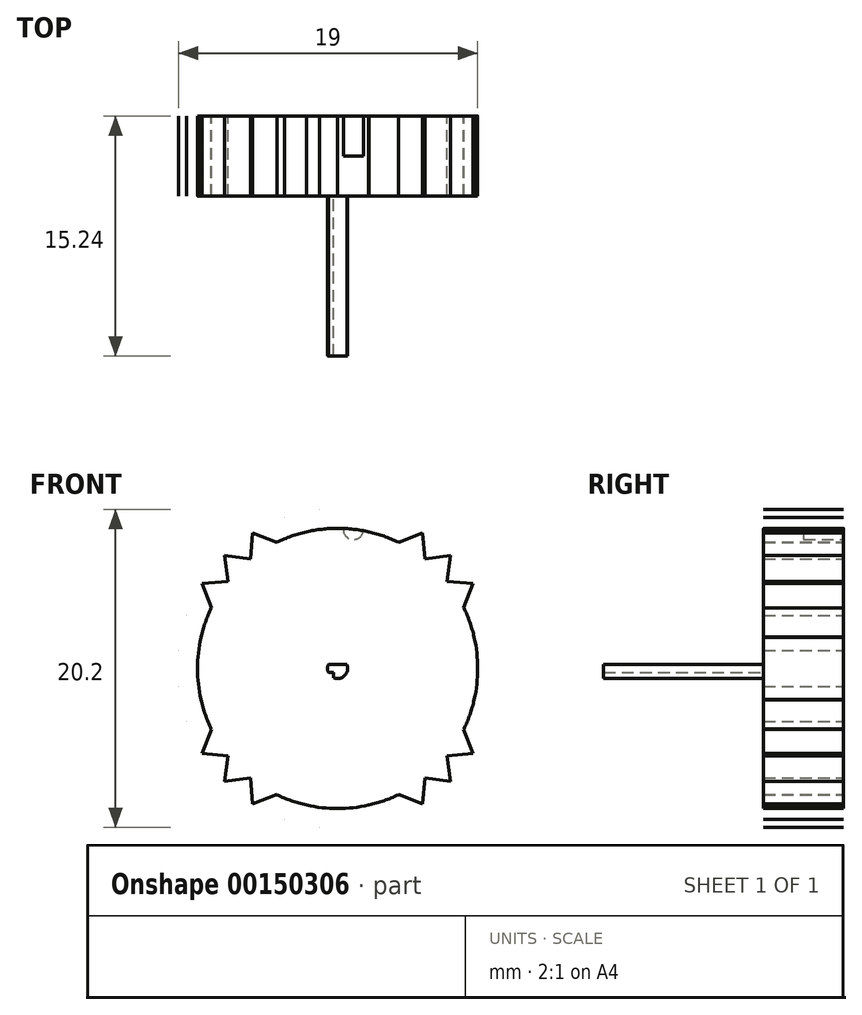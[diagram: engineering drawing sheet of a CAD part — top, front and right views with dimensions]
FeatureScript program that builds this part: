
annotation { "Feature Type Name" : "Feature", "Feature Type Description" : "" }
export const myFeature = defineFeature(function(context is Context, id is Id, definition is map)
    precondition{}
    {
        {
            var Q0;
            Q0=qCreatedBy(makeId("Front.planeOp"),FACE);
            var sketch = newSketch(context, id + "F0", { "sketchPlane" : qUnion([Q0])});
            skCircle(sketch, "E0", {"center": v(0, 0) * mm, "radius": 10.16 * mm});
            skCircle(sketch, "E1", {"center": v(0, 0) * mm, "radius": 8.9 * mm});
            skLineSegment(sketch, "E2", {"start": v(0, 0) * mm, "end": v(0, 8.9) * mm});
            skLineSegment(sketch, "E3", {"start": v(0, 8.9) * mm, "end": v(0, -8.9) * mm});
            skLineSegment(sketch, "E4", {"start": v(0, -8.9) * mm, "end": v(-1.14, -10.1) * mm});
            skLineSegment(sketch, "E5", {"start": v(-1.14, -10.1) * mm, "end": v(-1.98, -8.67) * mm});
            skLineSegment(sketch, "E6", {"start": v(-1.98, -8.67) * mm, "end": v(0, 0) * mm});
            skLineSegment(sketch, "E7", {"start": v(-1.14, -10.1) * mm, "end": v(0, 0) * mm});
            skLineSegment(sketch, "E8", {"start": v(0, 0) * mm, "end": v(-3.36, -9.59) * mm});
            skLineSegment(sketch, "E9", {"start": v(0, 0) * mm, "end": v(-3.86, -8) * mm});
            skLineSegment(sketch, "E10", {"start": v(-3.86, -8) * mm, "end": v(-3.36, -9.59) * mm});
            skLineSegment(sketch, "E11", {"start": v(-1.98, -8.67) * mm, "end": v(-3.36, -9.59) * mm});
            skLineSegment(sketch, "E12.MirrorCS", {"start": v(-3.86, -8) * mm, "end": v(-5.4, -8.6) * mm});
            skLineSegment(sketch, "E13.MirrorCS", {"start": v(0, 0) * mm, "end": v(-5.4, -8.6) * mm});
            skLineSegment(sketch, "E14.MirrorCS", {"start": v(-5.54, -6.95) * mm, "end": v(-5.4, -8.6) * mm});
            skLineSegment(sketch, "E15.MirrorCS", {"start": v(-7.18, -7.18) * mm, "end": v(-5.54, -6.95) * mm});
            skLineSegment(sketch, "E16.MirrorCS", {"start": v(-5.54, -6.95) * mm, "end": v(0, 0) * mm});
            skLineSegment(sketch, "E17.MirrorCS", {"start": v(-7.18, -7.18) * mm, "end": v(0, 0) * mm});
            skLineSegment(sketch, "E18.MirrorCS", {"start": v(-6.95, -5.54) * mm, "end": v(-7.18, -7.18) * mm});
            skLineSegment(sketch, "E19.MirrorCS", {"start": v(6.95, 5.54) * mm, "end": v(-6.95, -5.54) * mm});
            skLineSegment(sketch, "E20.MirrorCS", {"start": v(-6.95, -5.54) * mm, "end": v(-8.6, -5.4) * mm});
            skLineSegment(sketch, "E21.MirrorCS", {"start": v(-8.6, -5.4) * mm, "end": v(0, 0) * mm});
            skLineSegment(sketch, "E22.MirrorCS", {"start": v(-8.6, -5.4) * mm, "end": v(-8, -3.86) * mm});
            skLineSegment(sketch, "E23.MirrorCS", {"start": v(-8, -3.86) * mm, "end": v(0, 0) * mm});
            skLineSegment(sketch, "E24.MirrorCS", {"start": v(-8, -3.86) * mm, "end": v(-9.59, -3.36) * mm});
            skLineSegment(sketch, "E25.MirrorCS", {"start": v(0, 0) * mm, "end": v(-9.59, -3.36) * mm});
            skLineSegment(sketch, "E26.MirrorCS", {"start": v(-8.67, -1.98) * mm, "end": v(-9.59, -3.36) * mm});
            skLineSegment(sketch, "E27.MirrorCS", {"start": v(0, 0) * mm, "end": v(-8.67, -1.98) * mm});
            skLineSegment(sketch, "E28.MirrorCS", {"start": v(-8.67, -1.98) * mm, "end": v(-10.1, -1.14) * mm});
            skLineSegment(sketch, "E29.MirrorCS", {"start": v(0, 0) * mm, "end": v(-10.1, -1.14) * mm});
            skLineSegment(sketch, "E30.MirrorCS", {"start": v(-8.9, 0) * mm, "end": v(-10.1, -1.14) * mm});
            skLineSegment(sketch, "E31.MirrorCS", {"start": v(-8.9, 0) * mm, "end": v(0, 0) * mm});
            skLineSegment(sketch, "E32.MirrorCS", {"start": v(-10.1, 1.14) * mm, "end": v(-8.9, 0) * mm});
            skLineSegment(sketch, "E33.MirrorCS", {"start": v(-10.1, 1.14) * mm, "end": v(0, 0) * mm});
            skLineSegment(sketch, "E34.MirrorCS", {"start": v(-8.67, 1.98) * mm, "end": v(-10.1, 1.14) * mm});
            skLineSegment(sketch, "E35.MirrorCS", {"start": v(8.67, -1.98) * mm, "end": v(-8.67, 1.98) * mm});
            skLineSegment(sketch, "E36.MirrorCS", {"start": v(-8.67, 1.98) * mm, "end": v(-9.59, 3.36) * mm});
            skLineSegment(sketch, "E37.MirrorCS", {"start": v(-9.59, 3.36) * mm, "end": v(0, 0) * mm});
            skLineSegment(sketch, "E38.MirrorCS", {"start": v(-9.59, 3.36) * mm, "end": v(-8, 3.86) * mm});
            skLineSegment(sketch, "E39.MirrorCS", {"start": v(-8, 3.86) * mm, "end": v(0, 0) * mm});
            skLineSegment(sketch, "E40.MirrorCS", {"start": v(-8, 3.86) * mm, "end": v(-8.6, 5.4) * mm});
            skLineSegment(sketch, "E41.MirrorCS", {"start": v(0, 0) * mm, "end": v(-8.6, 5.4) * mm});
            skLineSegment(sketch, "E42.MirrorCS", {"start": v(-6.95, 5.54) * mm, "end": v(-8.6, 5.4) * mm});
            skLineSegment(sketch, "E43.MirrorCS", {"start": v(0, 0) * mm, "end": v(-6.95, 5.54) * mm});
            skLineSegment(sketch, "E44.MirrorCS", {"start": v(-6.95, 5.54) * mm, "end": v(-7.18, 7.18) * mm});
            skLineSegment(sketch, "E45.MirrorCS", {"start": v(0, 0) * mm, "end": v(-7.18, 7.18) * mm});
            skLineSegment(sketch, "E46.MirrorCS", {"start": v(-5.54, 6.95) * mm, "end": v(-7.18, 7.18) * mm});
            skLineSegment(sketch, "E47.MirrorCS", {"start": v(-5.54, 6.95) * mm, "end": v(0, 0) * mm});
            skLineSegment(sketch, "E48.MirrorCS", {"start": v(-5.4, 8.6) * mm, "end": v(-5.54, 6.95) * mm});
            skLineSegment(sketch, "E49.MirrorCS", {"start": v(-5.4, 8.6) * mm, "end": v(0, 0) * mm});
            skLineSegment(sketch, "E50.MirrorCS", {"start": v(-3.86, 8) * mm, "end": v(-5.4, 8.6) * mm});
            skLineSegment(sketch, "E51.MirrorCS", {"start": v(3.86, -8) * mm, "end": v(-3.86, 8) * mm});
            skLineSegment(sketch, "E52.MirrorCS", {"start": v(-3.86, 8) * mm, "end": v(-3.36, 9.59) * mm});
            skLineSegment(sketch, "E53.MirrorCS", {"start": v(-3.36, 9.59) * mm, "end": v(0, 0) * mm});
            skLineSegment(sketch, "E54.MirrorCS", {"start": v(-3.36, 9.59) * mm, "end": v(-1.98, 8.67) * mm});
            skLineSegment(sketch, "E55.MirrorCS", {"start": v(-1.98, 8.67) * mm, "end": v(0, 0) * mm});
            skLineSegment(sketch, "E56.MirrorCS", {"start": v(-1.98, 8.67) * mm, "end": v(-1.14, 10.1) * mm});
            skLineSegment(sketch, "E57.MirrorCS", {"start": v(0, 0) * mm, "end": v(-1.14, 10.1) * mm});
            skLineSegment(sketch, "E58.MirrorCS", {"start": v(0, 8.89) * mm, "end": v(-1.14, 10.1) * mm});
            skLineSegment(sketch, "E59.MirrorCS", {"start": v(0, 0) * mm, "end": v(0, 8.89) * mm});
            skLineSegment(sketch, "E60.MirrorCS", {"start": v(0, 8.89) * mm, "end": v(1.14, 10.1) * mm});
            skLineSegment(sketch, "E61.MirrorCS", {"start": v(0, 0) * mm, "end": v(1.14, 10.1) * mm});
            skLineSegment(sketch, "E62.MirrorCS", {"start": v(1.98, 8.67) * mm, "end": v(1.14, 10.1) * mm});
            skLineSegment(sketch, "E63.MirrorCS", {"start": v(1.98, 8.67) * mm, "end": v(0, 0) * mm});
            skLineSegment(sketch, "E64.MirrorCS", {"start": v(3.36, 9.59) * mm, "end": v(1.98, 8.67) * mm});
            skLineSegment(sketch, "E65.MirrorCS", {"start": v(3.36, 9.59) * mm, "end": v(0, 0) * mm});
            skLineSegment(sketch, "E66.MirrorCS", {"start": v(3.86, 8) * mm, "end": v(3.36, 9.59) * mm});
            skLineSegment(sketch, "E67.MirrorCS", {"start": v(-3.86, -8) * mm, "end": v(3.86, 8) * mm});
            skLineSegment(sketch, "E68.MirrorCS", {"start": v(3.86, 8) * mm, "end": v(5.4, 8.6) * mm});
            skLineSegment(sketch, "E69.MirrorCS", {"start": v(5.4, 8.6) * mm, "end": v(0, 0) * mm});
            skLineSegment(sketch, "E70.MirrorCS", {"start": v(5.4, 8.6) * mm, "end": v(5.54, 6.95) * mm});
            skLineSegment(sketch, "E71.MirrorCS", {"start": v(5.54, 6.95) * mm, "end": v(0, 0) * mm});
            skLineSegment(sketch, "E72.MirrorCS", {"start": v(5.54, 6.95) * mm, "end": v(7.18, 7.18) * mm});
            skLineSegment(sketch, "E73.MirrorCS", {"start": v(0, 0) * mm, "end": v(7.18, 7.18) * mm});
            skLineSegment(sketch, "E74.MirrorCS", {"start": v(6.95, 5.54) * mm, "end": v(7.18, 7.18) * mm});
            skLineSegment(sketch, "E75.MirrorCS", {"start": v(6.95, 5.54) * mm, "end": v(8.6, 5.4) * mm});
            skLineSegment(sketch, "E76.MirrorCS", {"start": v(0, 0) * mm, "end": v(8.6, 5.4) * mm});
            skLineSegment(sketch, "E77.MirrorCS", {"start": v(8, 3.86) * mm, "end": v(8.6, 5.4) * mm});
            skLineSegment(sketch, "E78.MirrorCS", {"start": v(8, 3.86) * mm, "end": v(0, 0) * mm});
            skLineSegment(sketch, "E79.MirrorCS", {"start": v(9.59, 3.36) * mm, "end": v(8, 3.86) * mm});
            skLineSegment(sketch, "E80.MirrorCS", {"start": v(9.59, 3.36) * mm, "end": v(0, 0) * mm});
            skLineSegment(sketch, "E81.MirrorCS", {"start": v(8.67, 1.98) * mm, "end": v(9.59, 3.36) * mm});
            skLineSegment(sketch, "E82.MirrorCS", {"start": v(-8.67, -1.98) * mm, "end": v(8.67, 1.98) * mm});
            skLineSegment(sketch, "E83.MirrorCS", {"start": v(8.67, 1.98) * mm, "end": v(10.1, 1.14) * mm});
            skLineSegment(sketch, "E84.MirrorCS", {"start": v(10.1, 1.14) * mm, "end": v(8.9, 0) * mm});
            skLineSegment(sketch, "E85.MirrorCS", {"start": v(10.1, 1.14) * mm, "end": v(0, 0) * mm});
            skLineSegment(sketch, "E86.MirrorCS", {"start": v(8.9, 0) * mm, "end": v(0, 0) * mm});
            skLineSegment(sketch, "E87.MirrorCS", {"start": v(8.9, 0) * mm, "end": v(10.1, -1.14) * mm});
            skLineSegment(sketch, "E88.MirrorCS", {"start": v(0, 0) * mm, "end": v(10.1, -1.14) * mm});
            skLineSegment(sketch, "E89.MirrorCS", {"start": v(8.67, -1.98) * mm, "end": v(10.1, -1.14) * mm});
            skLineSegment(sketch, "E90.MirrorCS", {"start": v(0, 0) * mm, "end": v(8.67, -1.98) * mm});
            skLineSegment(sketch, "E91.MirrorCS", {"start": v(8.67, -1.98) * mm, "end": v(9.59, -3.36) * mm});
            skLineSegment(sketch, "E92.MirrorCS", {"start": v(0, 0) * mm, "end": v(9.59, -3.36) * mm});
            skLineSegment(sketch, "E93.MirrorCS", {"start": v(8, -3.86) * mm, "end": v(9.59, -3.36) * mm});
            skLineSegment(sketch, "E94.MirrorCS", {"start": v(8, -3.86) * mm, "end": v(0, 0) * mm});
            skLineSegment(sketch, "E95.MirrorCS", {"start": v(8.6, -5.4) * mm, "end": v(8, -3.86) * mm});
            skLineSegment(sketch, "E96.MirrorCS", {"start": v(8.6, -5.4) * mm, "end": v(0, 0) * mm});
            skLineSegment(sketch, "E97.MirrorCS", {"start": v(6.95, -5.54) * mm, "end": v(8.6, -5.4) * mm});
            skLineSegment(sketch, "E98.MirrorCS", {"start": v(-6.95, 5.54) * mm, "end": v(6.95, -5.54) * mm});
            skLineSegment(sketch, "E99.MirrorCS", {"start": v(6.95, -5.54) * mm, "end": v(7.18, -7.18) * mm});
            skLineSegment(sketch, "E100.MirrorCS", {"start": v(7.18, -7.18) * mm, "end": v(0, 0) * mm});
            skLineSegment(sketch, "E101.MirrorCS", {"start": v(7.18, -7.18) * mm, "end": v(5.54, -6.95) * mm});
            skLineSegment(sketch, "E102.MirrorCS", {"start": v(5.54, -6.95) * mm, "end": v(0, 0) * mm});
            skLineSegment(sketch, "E103.MirrorCS", {"start": v(5.54, -6.95) * mm, "end": v(5.4, -8.6) * mm});
            skLineSegment(sketch, "E104.MirrorCS", {"start": v(0, 0) * mm, "end": v(5.4, -8.6) * mm});
            skLineSegment(sketch, "E105.MirrorCS", {"start": v(3.86, -8) * mm, "end": v(5.4, -8.6) * mm});
            skLineSegment(sketch, "E106.MirrorCS", {"start": v(0, 0) * mm, "end": v(3.86, -8) * mm});
            skLineSegment(sketch, "E107.MirrorCS", {"start": v(3.86, -8) * mm, "end": v(3.36, -9.59) * mm});
            skLineSegment(sketch, "E108.MirrorCS", {"start": v(1.98, -8.67) * mm, "end": v(3.36, -9.59) * mm});
            skLineSegment(sketch, "E109.MirrorCS", {"start": v(0, 0) * mm, "end": v(3.36, -9.59) * mm});
            skLineSegment(sketch, "E110.MirrorCS", {"start": v(1.98, -8.67) * mm, "end": v(0, 0) * mm});
            skLineSegment(sketch, "E111.MirrorCS", {"start": v(1.14, -10.1) * mm, "end": v(1.98, -8.67) * mm});
            skLineSegment(sketch, "E112.MirrorCS", {"start": v(1.14, -10.1) * mm, "end": v(0, 0) * mm});
            skLineSegment(sketch, "E113.MirrorCS", {"start": v(0, -8.9) * mm, "end": v(1.14, -10.1) * mm});
            skSolve(sketch);
        }
        {
            var Q0;
            {var subQ0=sQuery(id+"F0.wireOp",EDGE,"E51.MirrorCS");Q0=makeQuery(id+"F0.imprint","IMPRINT",FACE,{"disambiguationData":[TD([[makeQuery(id+"F0.imprint","IMPRINT",EDGE,{"derivedFrom":subQ0}),1.0]])]});}
            var Q1;
            {var subQ0=sQuery(id+"F0.wireOp",EDGE,"E47.MirrorCS");Q1=makeQuery(id+"F0.imprint","IMPRINT",FACE,{"disambiguationData":[TD([[makeQuery(id+"F0.imprint","IMPRINT",EDGE,{"derivedFrom":subQ0}),1.0]])]});}
            var Q2;
            {var subQ0=sQuery(id+"F0.wireOp",EDGE,"E48.MirrorCS");Q2=makeQuery(id+"F0.imprint","IMPRINT",FACE,{"disambiguationData":[TD([[makeQuery(id+"F0.imprint","IMPRINT",EDGE,{"derivedFrom":subQ0}),1.0]])]});}
            var Q3;
            {var subQ0=sQuery(id+"F0.wireOp",EDGE,"E50.MirrorCS");Q3=makeQuery(id+"F0.imprint","IMPRINT",FACE,{"disambiguationData":[TD([[makeQuery(id+"F0.imprint","IMPRINT",EDGE,{"derivedFrom":subQ0}),1.0]])]});}
            var Q4;
            {var subQ0=sQuery(id+"F0.wireOp",EDGE,"E52.MirrorCS");Q4=makeQuery(id+"F0.imprint","IMPRINT",FACE,{"disambiguationData":[TD([[makeQuery(id+"F0.imprint","IMPRINT",EDGE,{"derivedFrom":subQ0}),-1.0]])]});}
            var Q5;
            {var subQ0=sQuery(id+"F0.wireOp",EDGE,"E54.MirrorCS");Q5=makeQuery(id+"F0.imprint","IMPRINT",FACE,{"disambiguationData":[TD([[makeQuery(id+"F0.imprint","IMPRINT",EDGE,{"derivedFrom":subQ0}),-1.0]])]});}
            var Q6;
            {var subQ0=sQuery(id+"F0.wireOp",EDGE,"E55.MirrorCS");Q6=makeQuery(id+"F0.imprint","IMPRINT",FACE,{"disambiguationData":[TD([[makeQuery(id+"F0.imprint","IMPRINT",EDGE,{"derivedFrom":subQ0}),-1.0]])]});}
            var Q7;
            {var subQ0=sQuery(id+"F0.wireOp",EDGE,"E51.MirrorCS");Q7=makeQuery(id+"F0.imprint","IMPRINT",FACE,{"disambiguationData":[TD([[makeQuery(id+"F0.imprint","IMPRINT",EDGE,{"derivedFrom":subQ0}),-1.0]])]});}
            var Q8;
            {var subQ1=sQuery(id+"F0.wireOp",EDGE,"E1");var subQ3=sQuery(id+"F0.wireOp",EDGE,"E57.MirrorCS");var subQ4=makeQuery(id+"F0.imprint","INTERSECT",VERTEX,{"derivedFrom":[subQ1,subQ3]});Q8=makeQuery(id+"F0.imprint","IMPRINT",FACE,{"disambiguationData":[TD([[makeQuery(id+"F0.imprint","IMPRINT",EDGE,{"disambiguationData":[TD([[subQ4,1.0]])],"derivedFrom":subQ1}),1.0]])]});}
            var Q9;
            {var subQ0=sQuery(id+"F0.wireOp",EDGE,"E58.MirrorCS");Q9=makeQuery(id+"F0.imprint","IMPRINT",FACE,{"disambiguationData":[TD([[makeQuery(id+"F0.imprint","IMPRINT",EDGE,{"derivedFrom":subQ0}),1.0]])]});}
            var Q10;
            {var subQ0=sQuery(id+"F0.wireOp",EDGE,"E56.MirrorCS");Q10=makeQuery(id+"F0.imprint","IMPRINT",FACE,{"disambiguationData":[TD([[makeQuery(id+"F0.imprint","IMPRINT",EDGE,{"derivedFrom":subQ0}),-1.0]])]});}
            var Q11;
            {var subQ0=sQuery(id+"F0.wireOp",EDGE,"E55.MirrorCS");Q11=makeQuery(id+"F0.imprint","IMPRINT",FACE,{"disambiguationData":[TD([[makeQuery(id+"F0.imprint","IMPRINT",EDGE,{"derivedFrom":subQ0}),1.0]])]});}
            var Q12;
            {var subQ0=sQuery(id+"F0.wireOp",EDGE,"E47.MirrorCS");Q12=makeQuery(id+"F0.imprint","IMPRINT",FACE,{"disambiguationData":[TD([[makeQuery(id+"F0.imprint","IMPRINT",EDGE,{"derivedFrom":subQ0}),-1.0]])]});}
            var Q13;
            {var subQ0=sQuery(id+"F0.wireOp",EDGE,"E46.MirrorCS");Q13=makeQuery(id+"F0.imprint","IMPRINT",FACE,{"disambiguationData":[TD([[makeQuery(id+"F0.imprint","IMPRINT",EDGE,{"derivedFrom":subQ0}),1.0]])]});}
            var Q14;
            {var subQ1=sQuery(id+"F0.wireOp",EDGE,"E1");var subQ3=sQuery(id+"F0.wireOp",EDGE,"E45.MirrorCS");var subQ4=makeQuery(id+"F0.imprint","INTERSECT",VERTEX,{"derivedFrom":[subQ1,subQ3]});Q14=makeQuery(id+"F0.imprint","IMPRINT",FACE,{"disambiguationData":[TD([[makeQuery(id+"F0.imprint","IMPRINT",EDGE,{"disambiguationData":[TD([[subQ4,-1.0]])],"derivedFrom":subQ1}),1.0]])]});}
            var Q15;
            {var subQ0=sQuery(id+"F0.wireOp",EDGE,"E44.MirrorCS");Q15=makeQuery(id+"F0.imprint","IMPRINT",FACE,{"disambiguationData":[TD([[makeQuery(id+"F0.imprint","IMPRINT",EDGE,{"derivedFrom":subQ0}),-1.0]])]});}
            var Q16;
            {var subQ1=sQuery(id+"F0.wireOp",EDGE,"E1");var subQ3=sQuery(id+"F0.wireOp",EDGE,"E41.MirrorCS");var subQ4=makeQuery(id+"F0.imprint","INTERSECT",VERTEX,{"derivedFrom":[subQ1,subQ3]});Q16=makeQuery(id+"F0.imprint","IMPRINT",FACE,{"disambiguationData":[TD([[makeQuery(id+"F0.imprint","IMPRINT",EDGE,{"disambiguationData":[TD([[subQ4,1.0]])],"derivedFrom":subQ1}),1.0]])]});}
            var Q17;
            {var subQ0=sQuery(id+"F0.wireOp",EDGE,"E42.MirrorCS");Q17=makeQuery(id+"F0.imprint","IMPRINT",FACE,{"disambiguationData":[TD([[makeQuery(id+"F0.imprint","IMPRINT",EDGE,{"derivedFrom":subQ0}),1.0]])]});}
            var Q18;
            {var subQ0=sQuery(id+"F0.wireOp",EDGE,"E40.MirrorCS");Q18=makeQuery(id+"F0.imprint","IMPRINT",FACE,{"disambiguationData":[TD([[makeQuery(id+"F0.imprint","IMPRINT",EDGE,{"derivedFrom":subQ0}),-1.0]])]});}
            var Q19;
            {var subQ0=sQuery(id+"F0.wireOp",EDGE,"E39.MirrorCS");Q19=makeQuery(id+"F0.imprint","IMPRINT",FACE,{"disambiguationData":[TD([[makeQuery(id+"F0.imprint","IMPRINT",EDGE,{"derivedFrom":subQ0}),1.0]])]});}
            var Q20;
            {var subQ0=sQuery(id+"F0.wireOp",EDGE,"E39.MirrorCS");Q20=makeQuery(id+"F0.imprint","IMPRINT",FACE,{"disambiguationData":[TD([[makeQuery(id+"F0.imprint","IMPRINT",EDGE,{"derivedFrom":subQ0}),-1.0]])]});}
            var Q21;
            {var subQ0=sQuery(id+"F0.wireOp",EDGE,"E38.MirrorCS");Q21=makeQuery(id+"F0.imprint","IMPRINT",FACE,{"disambiguationData":[TD([[makeQuery(id+"F0.imprint","IMPRINT",EDGE,{"derivedFrom":subQ0}),-1.0]])]});}
            var Q22;
            {var subQ0=sQuery(id+"F0.wireOp",EDGE,"E36.MirrorCS");Q22=makeQuery(id+"F0.imprint","IMPRINT",FACE,{"disambiguationData":[TD([[makeQuery(id+"F0.imprint","IMPRINT",EDGE,{"derivedFrom":subQ0}),-1.0]])]});}
            var Q23;
            {var subQ0=sQuery(id+"F0.wireOp",EDGE,"E35.MirrorCS");Q23=makeQuery(id+"F0.imprint","IMPRINT",FACE,{"disambiguationData":[TD([[makeQuery(id+"F0.imprint","IMPRINT",EDGE,{"derivedFrom":subQ0}),-1.0]])]});}
            var Q24;
            {var subQ0=sQuery(id+"F0.wireOp",EDGE,"E35.MirrorCS");Q24=makeQuery(id+"F0.imprint","IMPRINT",FACE,{"disambiguationData":[TD([[makeQuery(id+"F0.imprint","IMPRINT",EDGE,{"derivedFrom":subQ0}),1.0]])]});}
            var Q25;
            {var subQ0=sQuery(id+"F0.wireOp",EDGE,"E34.MirrorCS");Q25=makeQuery(id+"F0.imprint","IMPRINT",FACE,{"disambiguationData":[TD([[makeQuery(id+"F0.imprint","IMPRINT",EDGE,{"derivedFrom":subQ0}),1.0]])]});}
            var Q26;
            {var subQ0=sQuery(id+"F0.wireOp",EDGE,"E32.MirrorCS");Q26=makeQuery(id+"F0.imprint","IMPRINT",FACE,{"disambiguationData":[TD([[makeQuery(id+"F0.imprint","IMPRINT",EDGE,{"derivedFrom":subQ0}),1.0]])]});}
            var Q27;
            {var subQ0=sQuery(id+"F0.wireOp",EDGE,"E31.MirrorCS");Q27=makeQuery(id+"F0.imprint","IMPRINT",FACE,{"disambiguationData":[TD([[makeQuery(id+"F0.imprint","IMPRINT",EDGE,{"derivedFrom":subQ0}),1.0]])]});}
            var Q28;
            {var subQ0=sQuery(id+"F0.wireOp",EDGE,"E31.MirrorCS");Q28=makeQuery(id+"F0.imprint","IMPRINT",FACE,{"disambiguationData":[TD([[makeQuery(id+"F0.imprint","IMPRINT",EDGE,{"derivedFrom":subQ0}),-1.0]])]});}
            var Q29;
            {var subQ0=sQuery(id+"F0.wireOp",EDGE,"E30.MirrorCS");Q29=makeQuery(id+"F0.imprint","IMPRINT",FACE,{"disambiguationData":[TD([[makeQuery(id+"F0.imprint","IMPRINT",EDGE,{"derivedFrom":subQ0}),1.0]])]});}
            var Q30;
            {var subQ0=sQuery(id+"F0.wireOp",EDGE,"E28.MirrorCS");Q30=makeQuery(id+"F0.imprint","IMPRINT",FACE,{"disambiguationData":[TD([[makeQuery(id+"F0.imprint","IMPRINT",EDGE,{"derivedFrom":subQ0}),-1.0]])]});}
            var Q31;
            {var subQ1=sQuery(id+"F0.wireOp",EDGE,"E1");var subQ3=sQuery(id+"F0.wireOp",EDGE,"E29.MirrorCS");var subQ4=makeQuery(id+"F0.imprint","INTERSECT",VERTEX,{"derivedFrom":[subQ1,subQ3]});Q31=makeQuery(id+"F0.imprint","IMPRINT",FACE,{"disambiguationData":[TD([[makeQuery(id+"F0.imprint","IMPRINT",EDGE,{"disambiguationData":[TD([[subQ4,-1.0]])],"derivedFrom":subQ1}),1.0]])]});}
            var Q32;
            {var subQ1=sQuery(id+"F0.wireOp",EDGE,"E1");var subQ3=sQuery(id+"F0.wireOp",EDGE,"E25.MirrorCS");var subQ4=makeQuery(id+"F0.imprint","INTERSECT",VERTEX,{"derivedFrom":[subQ1,subQ3]});Q32=makeQuery(id+"F0.imprint","IMPRINT",FACE,{"disambiguationData":[TD([[makeQuery(id+"F0.imprint","IMPRINT",EDGE,{"disambiguationData":[TD([[subQ4,1.0]])],"derivedFrom":subQ1}),1.0]])]});}
            var Q33;
            {var subQ0=sQuery(id+"F0.wireOp",EDGE,"E26.MirrorCS");Q33=makeQuery(id+"F0.imprint","IMPRINT",FACE,{"disambiguationData":[TD([[makeQuery(id+"F0.imprint","IMPRINT",EDGE,{"derivedFrom":subQ0}),1.0]])]});}
            var Q34;
            {var subQ0=sQuery(id+"F0.wireOp",EDGE,"E24.MirrorCS");Q34=makeQuery(id+"F0.imprint","IMPRINT",FACE,{"disambiguationData":[TD([[makeQuery(id+"F0.imprint","IMPRINT",EDGE,{"derivedFrom":subQ0}),-1.0]])]});}
            var Q35;
            {var subQ0=sQuery(id+"F0.wireOp",EDGE,"E23.MirrorCS");Q35=makeQuery(id+"F0.imprint","IMPRINT",FACE,{"disambiguationData":[TD([[makeQuery(id+"F0.imprint","IMPRINT",EDGE,{"derivedFrom":subQ0}),1.0]])]});}
            var Q36;
            {var subQ0=sQuery(id+"F0.wireOp",EDGE,"E23.MirrorCS");Q36=makeQuery(id+"F0.imprint","IMPRINT",FACE,{"disambiguationData":[TD([[makeQuery(id+"F0.imprint","IMPRINT",EDGE,{"derivedFrom":subQ0}),-1.0]])]});}
            var Q37;
            {var subQ0=sQuery(id+"F0.wireOp",EDGE,"E22.MirrorCS");Q37=makeQuery(id+"F0.imprint","IMPRINT",FACE,{"disambiguationData":[TD([[makeQuery(id+"F0.imprint","IMPRINT",EDGE,{"derivedFrom":subQ0}),-1.0]])]});}
            var Q38;
            {var subQ0=sQuery(id+"F0.wireOp",EDGE,"E20.MirrorCS");Q38=makeQuery(id+"F0.imprint","IMPRINT",FACE,{"disambiguationData":[TD([[makeQuery(id+"F0.imprint","IMPRINT",EDGE,{"derivedFrom":subQ0}),-1.0]])]});}
            var Q39;
            {var subQ1=sQuery(id+"F0.wireOp",EDGE,"E1");var subQ3=sQuery(id+"F0.wireOp",EDGE,"E21.MirrorCS");var subQ4=makeQuery(id+"F0.imprint","INTERSECT",VERTEX,{"derivedFrom":[subQ1,subQ3]});Q39=makeQuery(id+"F0.imprint","IMPRINT",FACE,{"disambiguationData":[TD([[makeQuery(id+"F0.imprint","IMPRINT",EDGE,{"disambiguationData":[TD([[subQ4,-1.0]])],"derivedFrom":subQ1}),1.0]])]});}
            var Q40;
            {var subQ1=sQuery(id+"F0.wireOp",EDGE,"E1");var subQ3=sQuery(id+"F0.wireOp",EDGE,"E17.MirrorCS");var subQ4=makeQuery(id+"F0.imprint","INTERSECT",VERTEX,{"derivedFrom":[subQ1,subQ3]});Q40=makeQuery(id+"F0.imprint","IMPRINT",FACE,{"disambiguationData":[TD([[makeQuery(id+"F0.imprint","IMPRINT",EDGE,{"disambiguationData":[TD([[subQ4,1.0]])],"derivedFrom":subQ1}),1.0]])]});}
            var Q41;
            {var subQ0=sQuery(id+"F0.wireOp",EDGE,"E16.MirrorCS");Q41=makeQuery(id+"F0.imprint","IMPRINT",FACE,{"disambiguationData":[TD([[makeQuery(id+"F0.imprint","IMPRINT",EDGE,{"derivedFrom":subQ0}),1.0]])]});}
            var Q42;
            {var subQ0=sQuery(id+"F0.wireOp",EDGE,"E16.MirrorCS");Q42=makeQuery(id+"F0.imprint","IMPRINT",FACE,{"disambiguationData":[TD([[makeQuery(id+"F0.imprint","IMPRINT",EDGE,{"derivedFrom":subQ0}),-1.0]])]});}
            var Q43;
            {var subQ0=sQuery(id+"F0.wireOp",EDGE,"E18.MirrorCS");Q43=makeQuery(id+"F0.imprint","IMPRINT",FACE,{"disambiguationData":[TD([[makeQuery(id+"F0.imprint","IMPRINT",EDGE,{"derivedFrom":subQ0}),1.0]])]});}
            var Q44;
            {var subQ0=sQuery(id+"F0.wireOp",EDGE,"E15.MirrorCS");Q44=makeQuery(id+"F0.imprint","IMPRINT",FACE,{"disambiguationData":[TD([[makeQuery(id+"F0.imprint","IMPRINT",EDGE,{"derivedFrom":subQ0}),1.0]])]});}
            var Q45;
            {var subQ0=sQuery(id+"F0.wireOp",EDGE,"E14.MirrorCS");Q45=makeQuery(id+"F0.imprint","IMPRINT",FACE,{"disambiguationData":[TD([[makeQuery(id+"F0.imprint","IMPRINT",EDGE,{"derivedFrom":subQ0}),1.0]])]});}
            var Q46;
            {var subQ0=sQuery(id+"F0.wireOp",EDGE,"E12.MirrorCS");Q46=makeQuery(id+"F0.imprint","IMPRINT",FACE,{"disambiguationData":[TD([[makeQuery(id+"F0.imprint","IMPRINT",EDGE,{"derivedFrom":subQ0}),-1.0]])]});}
            var Q47;
            {var subQ1=sQuery(id+"F0.wireOp",EDGE,"E1");var subQ3=sQuery(id+"F0.wireOp",EDGE,"E8");var subQ4=makeQuery(id+"F0.imprint","INTERSECT",VERTEX,{"derivedFrom":[subQ1,subQ3]});Q47=makeQuery(id+"F0.imprint","IMPRINT",FACE,{"disambiguationData":[TD([[makeQuery(id+"F0.imprint","IMPRINT",EDGE,{"disambiguationData":[TD([[subQ4,1.0]])],"derivedFrom":subQ1}),1.0]])]});}
            var Q48;
            {var subQ0=sQuery(id+"F0.wireOp",EDGE,"E10");Q48=makeQuery(id+"F0.imprint","IMPRINT",FACE,{"disambiguationData":[TD([[makeQuery(id+"F0.imprint","IMPRINT",EDGE,{"derivedFrom":subQ0}),1.0]])]});}
            var Q49;
            {var subQ0=sQuery(id+"F0.wireOp",EDGE,"E11");Q49=makeQuery(id+"F0.imprint","IMPRINT",FACE,{"disambiguationData":[TD([[makeQuery(id+"F0.imprint","IMPRINT",EDGE,{"derivedFrom":subQ0}),-1.0]])]});}
            var Q50;
            {var subQ0=sQuery(id+"F0.wireOp",EDGE,"E6");Q50=makeQuery(id+"F0.imprint","IMPRINT",FACE,{"disambiguationData":[TD([[makeQuery(id+"F0.imprint","IMPRINT",EDGE,{"derivedFrom":subQ0}),1.0]])]});}
            var Q51;
            {var subQ0=sQuery(id+"F0.wireOp",EDGE,"E6");Q51=makeQuery(id+"F0.imprint","IMPRINT",FACE,{"disambiguationData":[TD([[makeQuery(id+"F0.imprint","IMPRINT",EDGE,{"derivedFrom":subQ0}),-1.0]])]});}
            var Q52;
            {var subQ0=sQuery(id+"F0.wireOp",EDGE,"E4");Q52=makeQuery(id+"F0.imprint","IMPRINT",FACE,{"disambiguationData":[TD([[makeQuery(id+"F0.imprint","IMPRINT",EDGE,{"derivedFrom":subQ0}),-1.0]])]});}
            var Q53;
            {var subQ0=sQuery(id+"F0.wireOp",EDGE,"E5");Q53=makeQuery(id+"F0.imprint","IMPRINT",FACE,{"disambiguationData":[TD([[makeQuery(id+"F0.imprint","IMPRINT",EDGE,{"derivedFrom":subQ0}),-1.0]])]});}
            var Q54;
            {var subQ1=sQuery(id+"F0.wireOp",EDGE,"E1");var subQ3=sQuery(id+"F0.wireOp",EDGE,"E7");var subQ4=makeQuery(id+"F0.imprint","INTERSECT",VERTEX,{"derivedFrom":[subQ1,subQ3]});Q54=makeQuery(id+"F0.imprint","IMPRINT",FACE,{"disambiguationData":[TD([[makeQuery(id+"F0.imprint","IMPRINT",EDGE,{"disambiguationData":[TD([[subQ4,-1.0]])],"derivedFrom":subQ1}),1.0]])]});}
            var Q55;
            {var subQ1=sQuery(id+"F0.wireOp",EDGE,"E1");var subQ3=sQuery(id+"F0.wireOp",EDGE,"E13.MirrorCS");var subQ4=makeQuery(id+"F0.imprint","INTERSECT",VERTEX,{"derivedFrom":[subQ1,subQ3]});Q55=makeQuery(id+"F0.imprint","IMPRINT",FACE,{"disambiguationData":[TD([[makeQuery(id+"F0.imprint","IMPRINT",EDGE,{"disambiguationData":[TD([[subQ4,-1.0]])],"derivedFrom":subQ1}),1.0]])]});}
            extrude(context, id + "F1", {"entities" : qUnion([Q0, Q1, Q2, Q3, Q4, Q5, Q6, Q7, Q8, Q9, Q10, Q11, Q12, Q13, Q14, Q15, Q16, Q17, Q18, Q19, Q20, Q21, Q22, Q23, Q24, Q25, Q26, Q27, Q28, Q29, Q30, Q31, Q32, Q33, Q34, Q35, Q36, Q37, Q38, Q39, Q40, Q41, Q42, Q43, Q44, Q45, Q46, Q47, Q48, Q49, Q50, Q51, Q52, Q53, Q54, Q55]), "depth" : 5.08 * mm});
        }
        {
            var Q0;
            Q0=makeQuery(id+"F1.opExtrude","SWEPT_BODY",BODY,{"disambiguationData":[OSD([sQuery(id+"F0.wireOp",EDGE,"E4"),sQuery(id+"F0.wireOp",EDGE,"E5"),sQuery(id+"F0.wireOp",EDGE,"E10"),sQuery(id+"F0.wireOp",EDGE,"E11"),sQuery(id+"F0.wireOp",EDGE,"E12.MirrorCS"),sQuery(id+"F0.wireOp",EDGE,"E14.MirrorCS"),sQuery(id+"F0.wireOp",EDGE,"E15.MirrorCS"),sQuery(id+"F0.wireOp",EDGE,"E18.MirrorCS"),sQuery(id+"F0.wireOp",EDGE,"E20.MirrorCS"),sQuery(id+"F0.wireOp",EDGE,"E22.MirrorCS"),sQuery(id+"F0.wireOp",EDGE,"E24.MirrorCS"),sQuery(id+"F0.wireOp",EDGE,"E26.MirrorCS"),sQuery(id+"F0.wireOp",EDGE,"E28.MirrorCS"),sQuery(id+"F0.wireOp",EDGE,"E30.MirrorCS"),sQuery(id+"F0.wireOp",EDGE,"E32.MirrorCS"),sQuery(id+"F0.wireOp",EDGE,"E34.MirrorCS"),sQuery(id+"F0.wireOp",EDGE,"E36.MirrorCS"),sQuery(id+"F0.wireOp",EDGE,"E38.MirrorCS"),sQuery(id+"F0.wireOp",EDGE,"E40.MirrorCS"),sQuery(id+"F0.wireOp",EDGE,"E42.MirrorCS"),sQuery(id+"F0.wireOp",EDGE,"E44.MirrorCS"),sQuery(id+"F0.wireOp",EDGE,"E46.MirrorCS"),sQuery(id+"F0.wireOp",EDGE,"E48.MirrorCS"),sQuery(id+"F0.wireOp",EDGE,"E50.MirrorCS"),sQuery(id+"F0.wireOp",EDGE,"E52.MirrorCS"),sQuery(id+"F0.wireOp",EDGE,"E54.MirrorCS"),sQuery(id+"F0.wireOp",EDGE,"E56.MirrorCS"),sQuery(id+"F0.wireOp",EDGE,"E58.MirrorCS"),sQuery(id+"F0.wireOp",EDGE,"E3")])]});
            var Q1;
            Q1=qCreatedBy(makeId("Right.planeOp"),FACE);
            mirror(context, id + "F2", {"operationType" : NewBodyOperationType.ADD, "entities" : qUnion([Q0]), "mirrorPlane" : qUnion([Q1])});
        }
        {
            var Q0;
            {var subQ0=makeQuery(id+"F1.opExtrude","CAP_FACE",FACE,{"disambiguationData":[OSD([sQuery(id+"F0.wireOp",EDGE,"E4"),sQuery(id+"F0.wireOp",EDGE,"E5"),sQuery(id+"F0.wireOp",EDGE,"E10"),sQuery(id+"F0.wireOp",EDGE,"E11"),sQuery(id+"F0.wireOp",EDGE,"E12.MirrorCS"),sQuery(id+"F0.wireOp",EDGE,"E14.MirrorCS"),sQuery(id+"F0.wireOp",EDGE,"E15.MirrorCS"),sQuery(id+"F0.wireOp",EDGE,"E18.MirrorCS"),sQuery(id+"F0.wireOp",EDGE,"E20.MirrorCS"),sQuery(id+"F0.wireOp",EDGE,"E22.MirrorCS"),sQuery(id+"F0.wireOp",EDGE,"E24.MirrorCS"),sQuery(id+"F0.wireOp",EDGE,"E26.MirrorCS"),sQuery(id+"F0.wireOp",EDGE,"E28.MirrorCS"),sQuery(id+"F0.wireOp",EDGE,"E30.MirrorCS"),sQuery(id+"F0.wireOp",EDGE,"E32.MirrorCS"),sQuery(id+"F0.wireOp",EDGE,"E34.MirrorCS"),sQuery(id+"F0.wireOp",EDGE,"E36.MirrorCS"),sQuery(id+"F0.wireOp",EDGE,"E38.MirrorCS"),sQuery(id+"F0.wireOp",EDGE,"E40.MirrorCS"),sQuery(id+"F0.wireOp",EDGE,"E42.MirrorCS"),sQuery(id+"F0.wireOp",EDGE,"E44.MirrorCS"),sQuery(id+"F0.wireOp",EDGE,"E46.MirrorCS"),sQuery(id+"F0.wireOp",EDGE,"E48.MirrorCS"),sQuery(id+"F0.wireOp",EDGE,"E50.MirrorCS"),sQuery(id+"F0.wireOp",EDGE,"E52.MirrorCS"),sQuery(id+"F0.wireOp",EDGE,"E54.MirrorCS"),sQuery(id+"F0.wireOp",EDGE,"E56.MirrorCS"),sQuery(id+"F0.wireOp",EDGE,"E58.MirrorCS"),sQuery(id+"F0.wireOp",EDGE,"E3")])],"isStart":false});Q0=makeQuery(id+"F2.boolean.opBoolean","MERGE",FACE,{"derivedFrom":[subQ0,makeQuery(id+"F2.opPattern","COPY",FACE,{"derivedFrom":subQ0,"instanceName":"1"})]});}
            var sketch = newSketch(context, id + "F3", { "sketchPlane" : qUnion([Q0])});
            skCircle(sketch, "E114", {"center": v(0, 0) * mm, "radius": 0.64 * mm});
            skLineSegment(sketch, "E115.bottom", {"start": v(1.18, 0.25) * mm, "end": v(-1.18, 0.25) * mm});
            skLineSegment(sketch, "E115.top", {"start": v(1.18, -0.25) * mm, "end": v(-1.18, -0.25) * mm});
            skLineSegment(sketch, "E115.left", {"start": v(1.18, 0.25) * mm, "end": v(1.18, -0.25) * mm});
            skLineSegment(sketch, "E115.right", {"start": v(-1.18, 0.25) * mm, "end": v(-1.18, -0.25) * mm});
            skLineSegment(sketch, "E116.bottom", {"start": v(0.25, 1.07) * mm, "end": v(-0.25, 1.07) * mm});
            skLineSegment(sketch, "E116.top", {"start": v(0.25, -1.07) * mm, "end": v(-0.25, -1.07) * mm});
            skLineSegment(sketch, "E116.left", {"start": v(0.25, 1.07) * mm, "end": v(0.25, -1.07) * mm});
            skLineSegment(sketch, "E116.right", {"start": v(-0.25, 1.07) * mm, "end": v(-0.25, -1.07) * mm});
            skSolve(sketch);
        }
        {
            var Q0;
            {var subQ0=sQuery(id+"F3.wireOp",EDGE,"E116.left");var subQ1=sQuery(id+"F3.wireOp",EDGE,"E114");var subQ2=makeQuery(id+"F3.imprint","INTERSECT",VERTEX,{"disambiguationData":[OD(0.0)],"derivedFrom":[subQ1,subQ0]});Q0=makeQuery(id+"F3.imprint","IMPRINT",FACE,{"disambiguationData":[TD([[makeQuery(id+"F3.imprint","IMPRINT",EDGE,{"disambiguationData":[TD([[subQ2,-1.0]])],"derivedFrom":subQ1}),1.0]])]});}
            var Q1;
            {var subQ0=sQuery(id+"F3.wireOp",EDGE,"E115.bottom");var subQ1=sQuery(id+"F3.wireOp",EDGE,"E114");var subQ2=makeQuery(id+"F3.imprint","INTERSECT",VERTEX,{"disambiguationData":[OD(1.0)],"derivedFrom":[subQ1,subQ0]});Q1=makeQuery(id+"F3.imprint","IMPRINT",FACE,{"disambiguationData":[TD([[makeQuery(id+"F3.imprint","IMPRINT",EDGE,{"disambiguationData":[TD([[subQ2,-1.0]])],"derivedFrom":subQ1}),1.0]])]});}
            var Q2;
            {var subQ0=sQuery(id+"F3.wireOp",EDGE,"E116.left");var subQ1=sQuery(id+"F3.wireOp",EDGE,"E115.bottom");var subQ2=makeQuery(id+"F3.imprint","INTERSECT",VERTEX,{"derivedFrom":[subQ1,subQ0]});Q2=makeQuery(id+"F3.imprint","IMPRINT",FACE,{"disambiguationData":[TD([[makeQuery(id+"F3.imprint","IMPRINT",EDGE,{"disambiguationData":[TD([[subQ2,-1.0]])],"derivedFrom":subQ1}),1.0]])]});}
            var Q3;
            {var subQ0=sQuery(id+"F3.wireOp",EDGE,"E115.bottom");var subQ1=sQuery(id+"F3.wireOp",EDGE,"E114");var subQ2=makeQuery(id+"F3.imprint","INTERSECT",VERTEX,{"disambiguationData":[OD(0.0)],"derivedFrom":[subQ1,subQ0]});Q3=makeQuery(id+"F3.imprint","IMPRINT",FACE,{"disambiguationData":[TD([[makeQuery(id+"F3.imprint","IMPRINT",EDGE,{"disambiguationData":[TD([[subQ2,1.0]])],"derivedFrom":subQ1}),1.0]])]});}
            var Q4;
            {var subQ0=sQuery(id+"F3.wireOp",EDGE,"E116.right");var subQ1=sQuery(id+"F3.wireOp",EDGE,"E114");var subQ2=makeQuery(id+"F3.imprint","INTERSECT",VERTEX,{"disambiguationData":[OD(1.0)],"derivedFrom":[subQ1,subQ0]});Q4=makeQuery(id+"F3.imprint","IMPRINT",FACE,{"disambiguationData":[TD([[makeQuery(id+"F3.imprint","IMPRINT",EDGE,{"disambiguationData":[TD([[subQ2,-1.0]])],"derivedFrom":subQ1}),1.0]])]});}
            extrude(context, id + "F4", {"entities" : qUnion([Q0, Q1, Q2, Q3, Q4]), "operationType" : NewBodyOperationType.ADD, "depth" : 10.16 * mm});
        }
        {
            var Q0;
            {var subQ0=makeQuery(id+"F1.opExtrude","CAP_FACE",FACE,{"disambiguationData":[OSD([sQuery(id+"F0.wireOp",EDGE,"E4"),sQuery(id+"F0.wireOp",EDGE,"E5"),sQuery(id+"F0.wireOp",EDGE,"E10"),sQuery(id+"F0.wireOp",EDGE,"E11"),sQuery(id+"F0.wireOp",EDGE,"E12.MirrorCS"),sQuery(id+"F0.wireOp",EDGE,"E14.MirrorCS"),sQuery(id+"F0.wireOp",EDGE,"E15.MirrorCS"),sQuery(id+"F0.wireOp",EDGE,"E18.MirrorCS"),sQuery(id+"F0.wireOp",EDGE,"E20.MirrorCS"),sQuery(id+"F0.wireOp",EDGE,"E22.MirrorCS"),sQuery(id+"F0.wireOp",EDGE,"E24.MirrorCS"),sQuery(id+"F0.wireOp",EDGE,"E26.MirrorCS"),sQuery(id+"F0.wireOp",EDGE,"E28.MirrorCS"),sQuery(id+"F0.wireOp",EDGE,"E30.MirrorCS"),sQuery(id+"F0.wireOp",EDGE,"E32.MirrorCS"),sQuery(id+"F0.wireOp",EDGE,"E34.MirrorCS"),sQuery(id+"F0.wireOp",EDGE,"E36.MirrorCS"),sQuery(id+"F0.wireOp",EDGE,"E38.MirrorCS"),sQuery(id+"F0.wireOp",EDGE,"E40.MirrorCS"),sQuery(id+"F0.wireOp",EDGE,"E42.MirrorCS"),sQuery(id+"F0.wireOp",EDGE,"E44.MirrorCS"),sQuery(id+"F0.wireOp",EDGE,"E46.MirrorCS"),sQuery(id+"F0.wireOp",EDGE,"E48.MirrorCS"),sQuery(id+"F0.wireOp",EDGE,"E50.MirrorCS"),sQuery(id+"F0.wireOp",EDGE,"E52.MirrorCS"),sQuery(id+"F0.wireOp",EDGE,"E54.MirrorCS"),sQuery(id+"F0.wireOp",EDGE,"E56.MirrorCS"),sQuery(id+"F0.wireOp",EDGE,"E58.MirrorCS"),sQuery(id+"F0.wireOp",EDGE,"E3")])],"isStart":true});Q0=makeQuery(id+"F2.boolean.opBoolean","MERGE",FACE,{"derivedFrom":[subQ0,makeQuery(id+"F2.opPattern","COPY",FACE,{"derivedFrom":subQ0,"instanceName":"1"})]});}
            var sketch = newSketch(context, id + "F5", { "sketchPlane" : qUnion([Q0])});
            skLineSegment(sketch, "E117", {"start": v(0, 0) * mm, "end": v(-1, 8.83) * mm});
            skCircle(sketch, "E118", {"center": v(-1, 8.83) * mm, "radius": 0.64 * mm});
            skLineSegment(sketch, "E119", {"start": v(-8.9, 0) * mm, "end": v(0, 0) * mm});
            skSolve(sketch);
        }
        {
            var Q0;
            Q0 = qSketchRegion(id + "F5", true);
            extrude(context, id + "F6", {"entities" : qUnion([Q0]), "operationType" : NewBodyOperationType.REMOVE, "oppositeDirection" : true, "depth" : 2.54 * mm});
        }
    });
